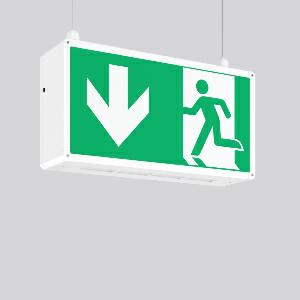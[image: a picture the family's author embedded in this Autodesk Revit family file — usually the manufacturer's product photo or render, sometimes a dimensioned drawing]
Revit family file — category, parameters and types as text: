
# Revit family: rechteck_seilpendel_671367_002_89_79db
name_source: partatom
category: Lighting Fixtures
units: mm (PartAtom-declared; Revit-internal decimal feet)

## family parameters
Cut with Voids When Loaded = No
Host = Face
Light Source = No
Part Type = Normal
Room Calculation Point = No
Round Connector Dimension = Use Diameter
Shared = No

## types (1)
- RECHTECK seilpendel
    Apparent Load = 0 VA
    Default Elevation = 1800 mm
    Description = Series: RECHTECK
Rectangular pendant luminaire in classic design. For escape route identification. Housing: aluminium, with plastic corner connectors. Display panels: plastic, opal, with motifs on one side/on both sides. Pendant luminaires (suspension provided on site) ready for connection to two suspension cables or chains. Driver integrated. Suitable for connection to central battery systems. With AC Control monitoring module for LUXIFAIR central battery units. Please indicate legend number when placing your order! 
Colour: white
Length: 485 mm
Width: 125 mm
Height: 250 mm
Weight: 2.65 kg
Operating mode: maintained power mode
Viewing Distance: 43 m
Lamp: LED
Socket: without socket
Colour temperature: 6500K
Colour rendering index (CRI): 70
System power: 9.1 W
Control gear: Regulated power supply
Protection class: I
Type of protection: IP 44
    Height = 250 mm
    Lamp = 0 x
    Length = 485 mm
    Luminous efficacy = 0 lm/W
    Manufacturer = RZB
    ModVariant = No
    Model = 671367.002.89
    Mounting Place = Ceiling
    Mounting Type = Pendant
    Number of Poles = 1
    OnlyDefault = Yes
    Power Factor = 1
    Product Name = RECHTECK seilpendel
    Product group = Pendant luminaires
    ProductGroupID = 902
    Protection Class = Protection class I
    Protection Degree = IP 44
    RLX_Detail_Level = 1
    RLX_Emergency_Light_Flux = 0 lm
    RLX_Emergency_Type = 0
    RLX_Emergency_Type_DB = No
    RlxData = <blob elided: 57097 chars, md5=b32edebc>
    Standby Power = 0 W
    System Light Flux = 0 lm
    System Power = 0 W
    Type Comments = Product without accessories
    Type Image = 671351.002.jpg
    URL = http://relux.com
    VarID = ---
    Voltage = 230 V
    Voltage Range = 220-240 V
    Weight = 0.00 kg
    Width = 125 mm

## geometry (parser evidence)
native form markers: Blend x4, Sweep x11
no freeform markers — native parametric forms only
